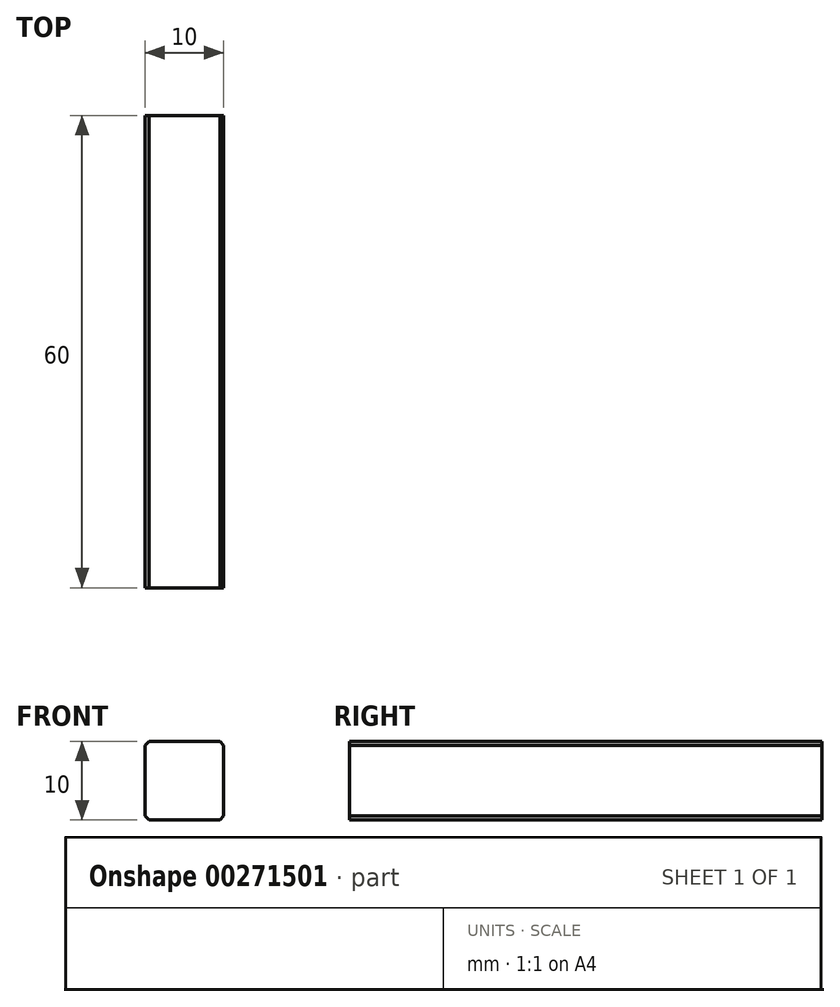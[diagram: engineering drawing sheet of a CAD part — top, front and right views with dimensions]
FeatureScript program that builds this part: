
annotation { "Feature Type Name" : "Feature", "Feature Type Description" : "" }
export const myFeature = defineFeature(function(context is Context, id is Id, definition is map)
    precondition{}
    {
        {
            var Q0;
            Q0=qCreatedBy(makeId("Front.planeOp"),FACE);
            var sketch = newSketch(context, id + "F0", { "sketchPlane" : qUnion([Q0])});
            skLineSegment(sketch, "E0.bottom", {"start": v(5, 5) * mm, "end": v(-5, 5) * mm});
            skLineSegment(sketch, "E0.top", {"start": v(5, -5) * mm, "end": v(-5, -5) * mm});
            skLineSegment(sketch, "E0.left", {"start": v(5, 5) * mm, "end": v(5, -5) * mm});
            skLineSegment(sketch, "E0.right", {"start": v(-5, 5) * mm, "end": v(-5, -5) * mm});
            skPoint(sketch, "E0.middle", {"position": v(0, 0) * mm});
            skSolve(sketch);
        }
        {
            var Q0;
            Q0 = qSketchRegion(id + "F0", true);
            extrude(context, id + "F1", {"entities" : qUnion([Q0]), "endBound" : BoundingType.SYMMETRIC, "depth" : 60 * mm});
        }
        {
            var Q0;
            Q0=makeQuery(id+"F1.opExtrude","SWEPT_EDGE",EDGE,{"disambiguationData":[OSD([sQuery(id+"F0.wireOp",EDGE,"E0.bottom"),sQuery(id+"F0.wireOp",EDGE,"E0.left")])]});
            var Q1;
            Q1=makeQuery(id+"F1.opExtrude","SWEPT_EDGE",EDGE,{"disambiguationData":[OSD([sQuery(id+"F0.wireOp",EDGE,"E0.top"),sQuery(id+"F0.wireOp",EDGE,"E0.left")])]});
            var Q2;
            Q2=makeQuery(id+"F1.opExtrude","SWEPT_EDGE",EDGE,{"disambiguationData":[OSD([sQuery(id+"F0.wireOp",EDGE,"E0.bottom"),sQuery(id+"F0.wireOp",EDGE,"E0.right")])]});
            var Q3;
            Q3=makeQuery(id+"F1.opExtrude","SWEPT_EDGE",EDGE,{"disambiguationData":[OSD([sQuery(id+"F0.wireOp",EDGE,"E0.top"),sQuery(id+"F0.wireOp",EDGE,"E0.right")])]});
            chamfer(context, id + "F2", {"entities" : qUnion([Q0, Q1, Q2, Q3]), "width" : 0.5 * mm, "tangentPropagation" : true});
        }
    });
